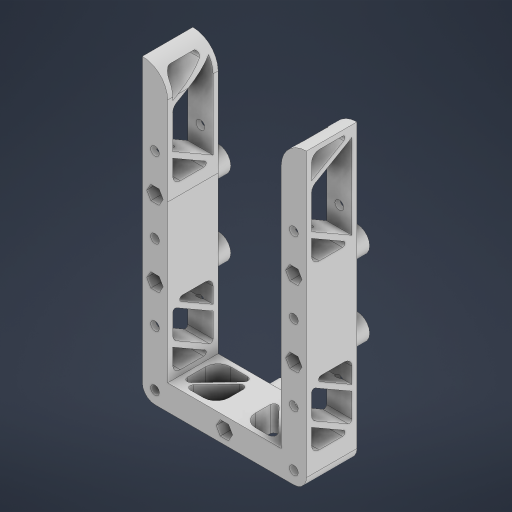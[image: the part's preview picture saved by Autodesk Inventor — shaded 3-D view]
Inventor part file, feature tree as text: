
AUTODESK INVENTOR PART (.ipt)
format: ipt  version: 2023 (Build 270158000, 158)  size: 650,752 bytes
history: native  units: mm
features: extrude x8, sketch x8, fillet x6, projected_geometry x5, plane x4, other x3, reference x1
ambient origin geometry x8: Origin, YZ Plane, XZ Plane, XY Plane, X Axis, Y Axis, Z Axis, Center Point
bodies: Body1 (feature_tree)
feature tree (35):
  plane  "Work Plane3"
  plane  "Work Plane4"
  plane  "Work Plane5"
  plane  "Work Plane6"
  extrude  "Extrusion3"  Depth=10.0mm
  extrude  "Extrusion4"  Depth=5.0mm TaperAngle=0.0deg
  extrude  "Extrusion5"  Depth=6.5mm
  fillet  "Fillet1"  Radius=60.0mm
  extrude  "Extrusion6"  Depth=60.0mm TaperAngle=360.0deg
  extrude  "Extrusion7"  Depth=60.0mm TaperAngle=360.0deg
  extrude  "Extrusion8"  Depth=5.0mm
  extrude  "Extrusion9"  Depth=45.0mm TaperAngle=0.0deg
  fillet  "Fillet2"  Radius=6.5mm
  fillet  "Fillet3"  Radius=60.0mm
  extrude  "Extrusion10"  Depth=1.0mm TaperAngle=360.0deg
  fillet  "Fillet4"  Radius=60.0mm
  fillet  "Fillet5"  Radius=3.0mm
  fillet  "Fillet6"  Radius=3.5mm
  sketch  "Sketch6"  dims[d38=10.0mm d39=6.5mm]
  reference  "Reference3"
  sketch  "Sketch7"  dims[d41=10.0mm d42=5.0mm d43=0.0mm]
  sketch  "Sketch8"  dims[d44=20.0mm d45=0.0mm d46=6.5mm d47=60.0mm d49=360.0deg]
  projected_geometry  "Projected Loop1"
  projected_geometry  "Projected Loop2"
  projected_geometry  "Projected Loop3"
  projected_geometry  "Projected Loop4"
  projected_geometry  "Projected Loop5"
  sketch  "Sketch9"  dims[d51=60.0mm d53=360.0deg d55=60.0mm d57=360.0deg]
  sketch  "Sketch10"  dims[d59=60.0mm d61=360.0deg d63=60.0mm d65=360.0deg]
  sketch  "Sketch11"  dims[d67=5.0mm d68=0.0mm d70=5.0mm]
  sketch  "Sketch12"  dims[d71=45.0mm d72=11.25mm d73=0.0mm d74=6.5mm d75=60.0mm d77=360.0deg]
  sketch  "Sketch13"  dims[d79=60.0mm d81=360.0deg d83=60.0mm d85=360.0deg d87=60.0mm d89=360.0deg d91=3.0mm d92=0.0mm d93=3.5mm d94=30.0mm d95=30.0mm d96=3.0mm d97=0.0mm d98=2.0mm d99=2.0mm d100=2.0mm d101=2.0mm d103=1.0mm d104=10.0mm d105=0.0mm d106=5.0mm d107=1.5mm d108=2.0mm d109=2.0mm d110=30.0deg d111=2.0mm d112=2.0mm d113=2.0mm d114=2.0mm d115=10.0mm d116=0.0mm d117=2.0mm d119=30.0deg d120=2.0mm d121=2.0mm d122=30.0deg d123=2.0mm d124=3.0mm d125=3.0mm d126=1.0mm d127=0.0mm d128=0.0mm d129=0.0mm]
  parser-record x1  (decoder bookkeeping rows leaked as tree rows — omitted from the tree; the rows remain in map.json)
  other  "total.iam"
  other  "bottom:1"
note: 1 file-system path scrubbed to <path> (originals preserved in map.json)
